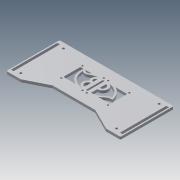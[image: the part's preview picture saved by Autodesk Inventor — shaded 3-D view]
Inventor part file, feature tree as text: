
AUTODESK INVENTOR PART (.ipt)
format: ipt  version: 2014 (Build 180170000, 170)  size: 260,096 bytes
history: native  units: mm
features: extrude x5, sketch x5, fillet x2
ambient origin geometry x8: Origin, YZ Plane, XZ Plane, XY Plane, X Axis, Y Axis, Z Axis, Center Point
bodies: Solid1 (feature_tree)
feature tree (12):
  extrude  "Extrusion1"  Depth=268.0mm
  extrude  "Extrusion2"  Depth=25.0mm
  extrude  "Extrusion5"  Depth=50.0mm
  fillet  "Fillet1"  Radius=3.0mm
  extrude  "Extrusion6"  Depth=21.5mm
  extrude  "Extrusion7"  Depth=12.5mm
  fillet  "Fillet2"  Radius=12.5mm
  sketch  "Sketch1"  dims[d1=125.0mm d2=268.0mm]
  sketch  "Sketch2"  dims[d4=6.0mm d5=0.0mm d6=25.0mm]
  sketch  "Sketch7"  dims[d7=34.0mm d9=50.0mm d10=3.0mm d11=0.0mm]
  sketch  "Sketch8"  dims[d47=34.0mm d48=21.5mm]
  sketch  "Sketch9"  dims[d49=21.5mm d50=12.5mm d51=12.5mm d56=2.875mm d57=6.25mm d58=2.875mm d60=8.0mm d61=5.4mm d62=108.9mm d63=10.0mm d64=0.0mm d65=2.0mm d66=8.1mm d67=50.0mm d68=60.0mm d69=100.0mm d70=25.0mm d71=4.3mm d72=10.0mm d73=0.0mm d74=4.0mm d75=40.0mm d76=50.0mm d77=25.0mm d78=12.5mm d79=5.0mm d80=8.0mm d81=22.0mm d82=15.0mm d83=34.0mm d84=9.0mm d85=4.0mm d86=4.0mm d87=55.0mm d88=8.0mm d89=5.0mm d90=10.0mm d91=5.0mm d92=34.0mm d93=35.0mm d94=20.0mm d95=6.0mm d96=55.0mm d97=4.0mm d99=4.0mm d100=10.0mm d101=0.0mm d102=2.0mm]
